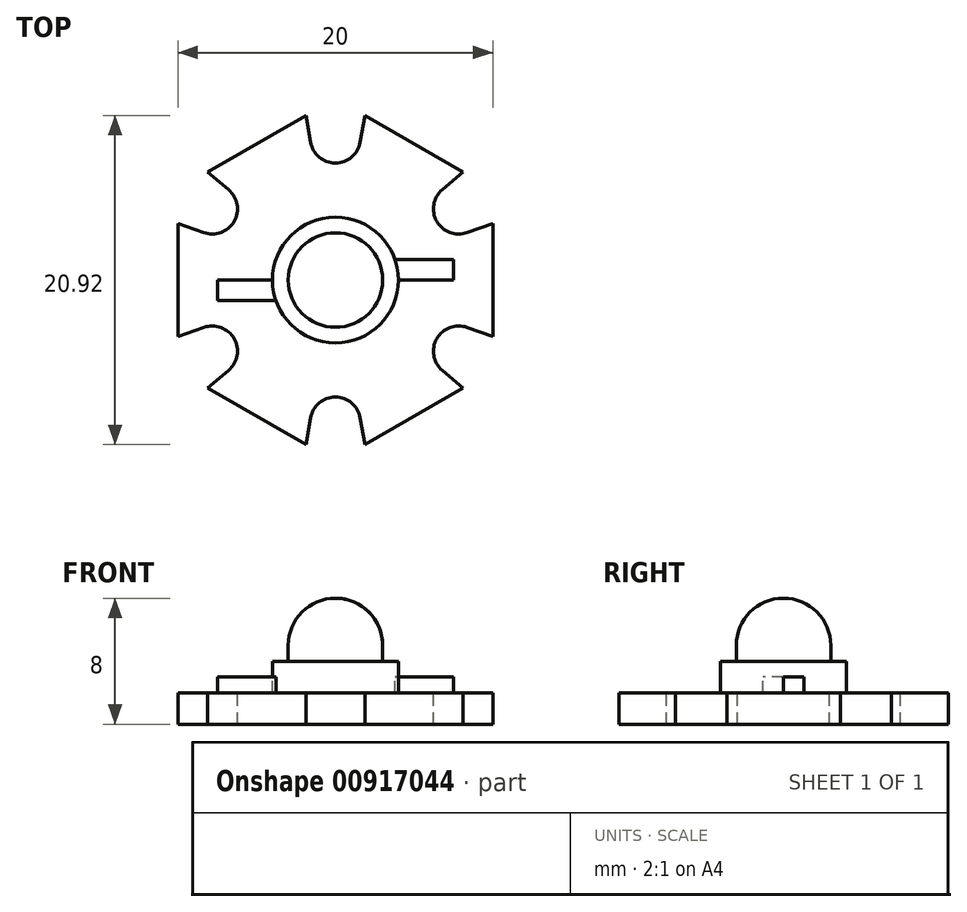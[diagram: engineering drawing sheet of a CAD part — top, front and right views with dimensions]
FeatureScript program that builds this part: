
annotation { "Feature Type Name" : "Feature", "Feature Type Description" : "" }
export const myFeature = defineFeature(function(context is Context, id is Id, definition is map)
    precondition{}
    {
        {
            var Q0;
            Q0=qCreatedBy(makeId("Top.planeOp"),FACE);
            var sketch = newSketch(context, id + "F0", { "sketchPlane" : qUnion([Q0])});
            skLineSegment(sketch, "E0", {"start": v(-10, 3.6) * mm, "end": v(-10, -3.6) * mm});
            skLineSegment(sketch, "E1", {"start": v(-10, -3.6) * mm, "end": v(0, 0) * mm});
            skLineSegment(sketch, "E2", {"start": v(0, 0) * mm, "end": v(-10, 3.6) * mm});
            skLineSegment(sketch, "E3.1.0", {"start": v(0, 0) * mm, "end": v(-8.12, -6.86) * mm});
            skLineSegment(sketch, "E3.1.1", {"start": v(-8.12, -6.86) * mm, "end": v(-1.88, -10.46) * mm});
            skLineSegment(sketch, "E3.1.2", {"start": v(-1.88, -10.46) * mm, "end": v(0, 0) * mm});
            skLineSegment(sketch, "E3.2.0", {"start": v(0, 0) * mm, "end": v(1.88, -10.46) * mm});
            skLineSegment(sketch, "E3.2.1", {"start": v(1.88, -10.46) * mm, "end": v(8.12, -6.86) * mm});
            skLineSegment(sketch, "E3.2.2", {"start": v(8.12, -6.86) * mm, "end": v(0, 0) * mm});
            skLineSegment(sketch, "E3.3.0", {"start": v(0, 0) * mm, "end": v(10, -3.6) * mm});
            skLineSegment(sketch, "E3.3.1", {"start": v(10, -3.6) * mm, "end": v(10, 3.6) * mm});
            skLineSegment(sketch, "E3.3.2", {"start": v(10, 3.6) * mm, "end": v(0, 0) * mm});
            skLineSegment(sketch, "E3.4.0", {"start": v(0, 0) * mm, "end": v(8.12, 6.86) * mm});
            skLineSegment(sketch, "E3.4.1", {"start": v(8.12, 6.86) * mm, "end": v(1.88, 10.46) * mm});
            skLineSegment(sketch, "E3.4.2", {"start": v(1.88, 10.46) * mm, "end": v(0, 0) * mm});
            skLineSegment(sketch, "E3.5.0", {"start": v(0, 0) * mm, "end": v(-1.88, 10.46) * mm});
            skLineSegment(sketch, "E3.5.1", {"start": v(-1.88, 10.46) * mm, "end": v(-8.12, 6.86) * mm});
            skLineSegment(sketch, "E3.5.2", {"start": v(-8.12, 6.86) * mm, "end": v(0, 0) * mm});
            skPoint(sketch, "E3.center", {"position": v(0, 0) * mm});
            skCircle(sketch, "E4", {"center": v(0, 9.03) * mm, "radius": 1.6 * mm});
            skCircle(sketch, "E5.1.0", {"center": v(-7.82, 4.52) * mm, "radius": 1.6 * mm});
            skCircle(sketch, "E5.2.0", {"center": v(-7.82, -4.52) * mm, "radius": 1.6 * mm});
            skCircle(sketch, "E5.3.0", {"center": v(0, -9.03) * mm, "radius": 1.6 * mm});
            skCircle(sketch, "E5.4.0", {"center": v(7.82, -4.52) * mm, "radius": 1.6 * mm});
            skCircle(sketch, "E5.5.0", {"center": v(7.82, 4.52) * mm, "radius": 1.6 * mm});
            skSolve(sketch);
        }
        {
            var Q0;
            {var subQ1=sQuery(id+"F0.wireOp",EDGE,"E3.5.1");Q0=makeQuery(id+"F0.imprint","IMPRINT",FACE,{"disambiguationData":[TD([[makeQuery(id+"F0.imprint","IMPRINT",EDGE,{"derivedFrom":subQ1}),1.0]])]});}
            var Q1;
            {var subQ1=sQuery(id+"F0.wireOp",EDGE,"E3.4.2");var subQ3=sQuery(id+"F0.wireOp",EDGE,"E4");var subQ4=makeQuery(id+"F0.imprint","INTERSECT",VERTEX,{"derivedFrom":[subQ1,subQ3]});Q1=makeQuery(id+"F0.imprint","IMPRINT",FACE,{"disambiguationData":[TD([[makeQuery(id+"F0.imprint","IMPRINT",EDGE,{"disambiguationData":[TD([[subQ4,1.0]])],"derivedFrom":subQ3}),-1.0]])]});}
            var Q2;
            {var subQ1=sQuery(id+"F0.wireOp",EDGE,"E3.4.1");Q2=makeQuery(id+"F0.imprint","IMPRINT",FACE,{"disambiguationData":[TD([[makeQuery(id+"F0.imprint","IMPRINT",EDGE,{"derivedFrom":subQ1}),1.0]])]});}
            var Q3;
            {var subQ1=sQuery(id+"F0.wireOp",EDGE,"E3.3.2");var subQ3=sQuery(id+"F0.wireOp",EDGE,"E5.5.0");var subQ4=makeQuery(id+"F0.imprint","INTERSECT",VERTEX,{"derivedFrom":[subQ1,subQ3]});Q3=makeQuery(id+"F0.imprint","IMPRINT",FACE,{"disambiguationData":[TD([[makeQuery(id+"F0.imprint","IMPRINT",EDGE,{"disambiguationData":[TD([[subQ4,1.0]])],"derivedFrom":subQ3}),-1.0]])]});}
            var Q4;
            {var subQ1=sQuery(id+"F0.wireOp",EDGE,"E3.3.1");Q4=makeQuery(id+"F0.imprint","IMPRINT",FACE,{"disambiguationData":[TD([[makeQuery(id+"F0.imprint","IMPRINT",EDGE,{"derivedFrom":subQ1}),1.0]])]});}
            var Q5;
            {var subQ1=sQuery(id+"F0.wireOp",EDGE,"E3.2.2");var subQ3=sQuery(id+"F0.wireOp",EDGE,"E5.4.0");var subQ4=makeQuery(id+"F0.imprint","INTERSECT",VERTEX,{"derivedFrom":[subQ1,subQ3]});Q5=makeQuery(id+"F0.imprint","IMPRINT",FACE,{"disambiguationData":[TD([[makeQuery(id+"F0.imprint","IMPRINT",EDGE,{"disambiguationData":[TD([[subQ4,1.0]])],"derivedFrom":subQ3}),-1.0]])]});}
            var Q6;
            {var subQ1=sQuery(id+"F0.wireOp",EDGE,"E3.2.1");Q6=makeQuery(id+"F0.imprint","IMPRINT",FACE,{"disambiguationData":[TD([[makeQuery(id+"F0.imprint","IMPRINT",EDGE,{"derivedFrom":subQ1}),1.0]])]});}
            var Q7;
            {var subQ1=sQuery(id+"F0.wireOp",EDGE,"E3.1.2");var subQ3=sQuery(id+"F0.wireOp",EDGE,"E5.3.0");var subQ4=makeQuery(id+"F0.imprint","INTERSECT",VERTEX,{"derivedFrom":[subQ1,subQ3]});Q7=makeQuery(id+"F0.imprint","IMPRINT",FACE,{"disambiguationData":[TD([[makeQuery(id+"F0.imprint","IMPRINT",EDGE,{"disambiguationData":[TD([[subQ4,1.0]])],"derivedFrom":subQ3}),-1.0]])]});}
            var Q8;
            {var subQ1=sQuery(id+"F0.wireOp",EDGE,"E3.1.1");Q8=makeQuery(id+"F0.imprint","IMPRINT",FACE,{"disambiguationData":[TD([[makeQuery(id+"F0.imprint","IMPRINT",EDGE,{"derivedFrom":subQ1}),1.0]])]});}
            var Q9;
            {var subQ1=sQuery(id+"F0.wireOp",EDGE,"E1");var subQ3=sQuery(id+"F0.wireOp",EDGE,"E5.2.0");var subQ4=makeQuery(id+"F0.imprint","INTERSECT",VERTEX,{"derivedFrom":[subQ1,subQ3]});Q9=makeQuery(id+"F0.imprint","IMPRINT",FACE,{"disambiguationData":[TD([[makeQuery(id+"F0.imprint","IMPRINT",EDGE,{"disambiguationData":[TD([[subQ4,1.0]])],"derivedFrom":subQ3}),-1.0]])]});}
            var Q10;
            {var subQ5=sQuery(id+"F0.wireOp",EDGE,"E0");Q10=makeQuery(id+"F0.imprint","IMPRINT",FACE,{"disambiguationData":[TD([[makeQuery(id+"F0.imprint","IMPRINT",EDGE,{"derivedFrom":subQ5}),1.0]])]});}
            var Q11;
            {var subQ1=sQuery(id+"F0.wireOp",EDGE,"E2");var subQ3=sQuery(id+"F0.wireOp",EDGE,"E5.1.0");var subQ4=makeQuery(id+"F0.imprint","INTERSECT",VERTEX,{"derivedFrom":[subQ1,subQ3]});Q11=makeQuery(id+"F0.imprint","IMPRINT",FACE,{"disambiguationData":[TD([[makeQuery(id+"F0.imprint","IMPRINT",EDGE,{"disambiguationData":[TD([[subQ4,-1.0]])],"derivedFrom":subQ3}),-1.0]])]});}
            extrude(context, id + "F1", {"entities" : qUnion([Q0, Q1, Q2, Q3, Q4, Q5, Q6, Q7, Q8, Q9, Q10, Q11]), "oppositeDirection" : true, "depth" : 2 * mm, "offsetDistance" : 25 * mm});
        }
        {
            var Q0;
            Q0=qCreatedBy(makeId("Front.planeOp"),FACE);
            var sketch = newSketch(context, id + "F2", { "sketchPlane" : qUnion([Q0])});
            skLineSegment(sketch, "E6", {"start": v(0, 0) * mm, "end": v(-4, 0) * mm});
            skLineSegment(sketch, "E7", {"start": v(-4, 0) * mm, "end": v(-4, 2) * mm});
            skLineSegment(sketch, "E8", {"start": v(-4, 2) * mm, "end": v(-3, 2) * mm});
            skLineSegment(sketch, "E9", {"start": v(-3, 2) * mm, "end": v(-3, 3) * mm});
            skLineSegment(sketch, "E10", {"start": v(0, 6) * mm, "end": v(0, 6) * mm});
            skLineSegment(sketch, "E11", {"start": v(0, 6) * mm, "end": v(0, 0) * mm});
            skPoint(sketch, "E12.visualSharp", {"position": v(-3, 6) * mm});
            skArc(sketch, "E12.filletArc", {"start": v(0, 6) * mm, "mid": v(-2.12, 5.12) * mm, "end": v(-3, 3) * mm});
            skSolve(sketch);
        }
        {
            var Q0;
            Q0=makeQuery(id+"F2.imprint","IMPRINT",FACE,{"disambiguationData":[TD([[makeQuery(id+"F2.imprint","IMPRINT",EDGE,{"derivedFrom":sQuery(id+"F2.wireOp",EDGE,"E6")}),-1.0]])]});
            var Q1;
            Q1=sQuery(id+"F2.wireOp",EDGE,"E11");
            revolve(context, id + "F3", {"operationType" : NewBodyOperationType.ADD, "surfaceOperationType" : NewSurfaceOperationType.NEW, "entities" : qUnion([Q0]), "axis" : qUnion([Q1]), "revolveType" : RevolveType.FULL});
        }
        {
            var Q0;
            Q0=makeQuery(id+"F1.opExtrude","CAP_FACE",FACE,{"disambiguationData":[OSD([sQuery(id+"F0.wireOp",EDGE,"E0"),sQuery(id+"F0.wireOp",EDGE,"E1"),sQuery(id+"F0.wireOp",EDGE,"E2"),sQuery(id+"F0.wireOp",EDGE,"E3.1.0"),sQuery(id+"F0.wireOp",EDGE,"E3.1.1"),sQuery(id+"F0.wireOp",EDGE,"E3.1.2"),sQuery(id+"F0.wireOp",EDGE,"E3.2.0"),sQuery(id+"F0.wireOp",EDGE,"E3.2.1"),sQuery(id+"F0.wireOp",EDGE,"E3.2.2"),sQuery(id+"F0.wireOp",EDGE,"E3.3.0"),sQuery(id+"F0.wireOp",EDGE,"E3.3.1"),sQuery(id+"F0.wireOp",EDGE,"E3.3.2"),sQuery(id+"F0.wireOp",EDGE,"E3.4.0"),sQuery(id+"F0.wireOp",EDGE,"E3.4.1"),sQuery(id+"F0.wireOp",EDGE,"E3.4.2"),sQuery(id+"F0.wireOp",EDGE,"E3.5.0"),sQuery(id+"F0.wireOp",EDGE,"E3.5.1"),sQuery(id+"F0.wireOp",EDGE,"E3.5.2"),sQuery(id+"F0.wireOp",EDGE,"E4"),sQuery(id+"F0.wireOp",EDGE,"E5.1.0"),sQuery(id+"F0.wireOp",EDGE,"E5.2.0"),sQuery(id+"F0.wireOp",EDGE,"E5.3.0"),sQuery(id+"F0.wireOp",EDGE,"E5.4.0"),sQuery(id+"F0.wireOp",EDGE,"E5.5.0")])],"isStart":true});
            var sketch = newSketch(context, id + "F4", { "sketchPlane" : qUnion([Q0])});
            skLineSegment(sketch, "E13.bottom", {"start": v(-3.4, 0) * mm, "end": v(-7.5, 0) * mm});
            skLineSegment(sketch, "E13.top", {"start": v(-3.4, -1.3) * mm, "end": v(-7.5, -1.3) * mm});
            skLineSegment(sketch, "E13.left", {"start": v(-3.4, 0) * mm, "end": v(-3.4, -1.3) * mm});
            skLineSegment(sketch, "E13.right", {"start": v(-7.5, 0) * mm, "end": v(-7.5, -1.3) * mm});
            skLineSegment(sketch, "E14.bottom", {"start": v(3.4, 0) * mm, "end": v(7.5, 0) * mm});
            skLineSegment(sketch, "E14.top", {"start": v(3.4, 1.3) * mm, "end": v(7.5, 1.3) * mm});
            skLineSegment(sketch, "E14.left", {"start": v(3.4, 0) * mm, "end": v(3.4, 1.3) * mm});
            skLineSegment(sketch, "E14.right", {"start": v(7.5, 0) * mm, "end": v(7.5, 1.3) * mm});
            skSolve(sketch);
        }
        {
            var Q0;
            Q0=makeQuery(id+"F4.imprint","IMPRINT",FACE,{"disambiguationData":[TD([[makeQuery(id+"F4.imprint","IMPRINT",EDGE,{"derivedFrom":sQuery(id+"F4.wireOp",EDGE,"E13.bottom")}),1.0]])]});
            var Q1;
            Q1=makeQuery(id+"F4.imprint","IMPRINT",FACE,{"disambiguationData":[TD([[makeQuery(id+"F4.imprint","IMPRINT",EDGE,{"derivedFrom":sQuery(id+"F4.wireOp",EDGE,"E14.bottom")}),1.0]])]});
            extrude(context, id + "F5", {"entities" : qUnion([Q0, Q1]), "operationType" : NewBodyOperationType.ADD, "depth" : 1 * mm, "offsetDistance" : 25 * mm});
        }
    });
